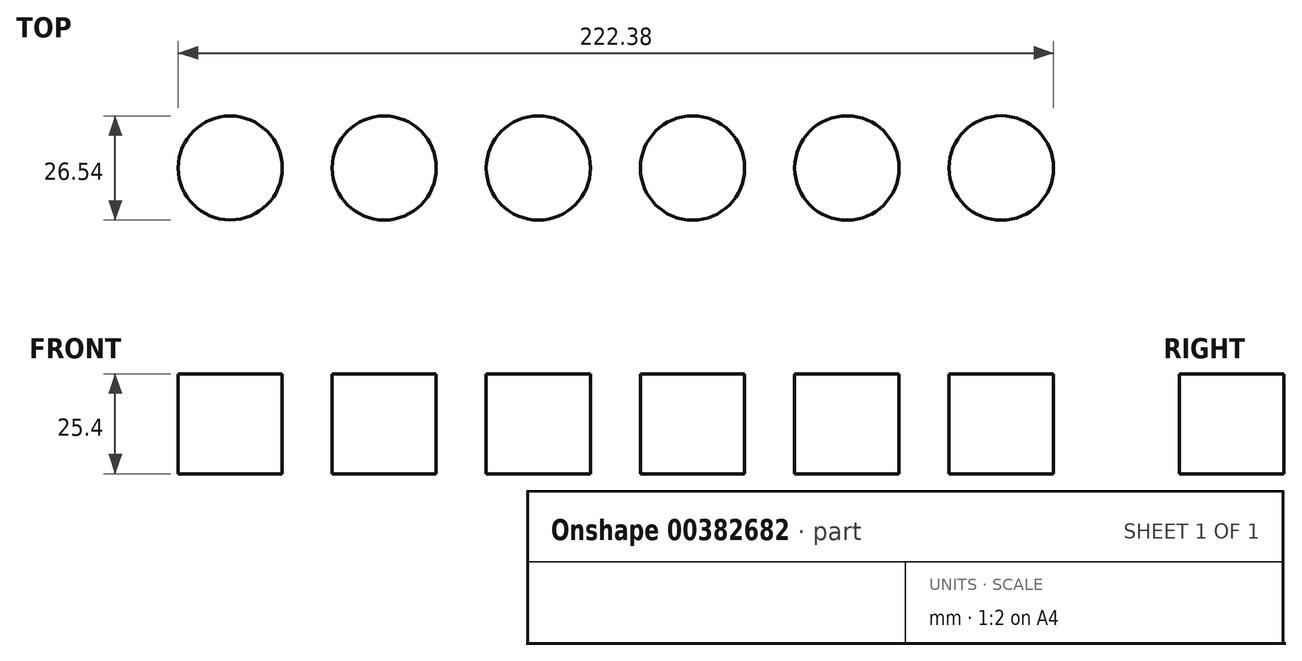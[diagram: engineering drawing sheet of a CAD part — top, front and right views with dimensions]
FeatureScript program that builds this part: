
annotation { "Feature Type Name" : "Feature", "Feature Type Description" : "" }
export const myFeature = defineFeature(function(context is Context, id is Id, definition is map)
    precondition{}
    {
        {
            var Q0;
            Q0=qCreatedBy(makeId("Top.planeOp"),FACE);
            var sketch = newSketch(context, id + "F0", { "sketchPlane" : qUnion([Q0])});
            skCircle(sketch, "E0", {"center": v(0, 0) * mm, "radius": 13.2 * mm});
            skCircle(sketch, "E1", {"center": v(39.13, 0) * mm, "radius": 13.22 * mm});
            skCircle(sketch, "E2", {"center": v(78.28, 0) * mm, "radius": 13.23 * mm});
            skCircle(sketch, "E3", {"center": v(117.46, 0) * mm, "radius": 13.25 * mm});
            skCircle(sketch, "E4", {"center": v(156.67, 0) * mm, "radius": 13.26 * mm});
            skCircle(sketch, "E5", {"center": v(195.9, 0) * mm, "radius": 13.27 * mm});
            skSolve(sketch);
        }
        {
            var Q0;
            Q0 = qSketchRegion(id + "F0", true);
            extrude(context, id + "F1", {"entities" : qUnion([Q0]), "depth" : 25.4 * mm});
        }
    });
